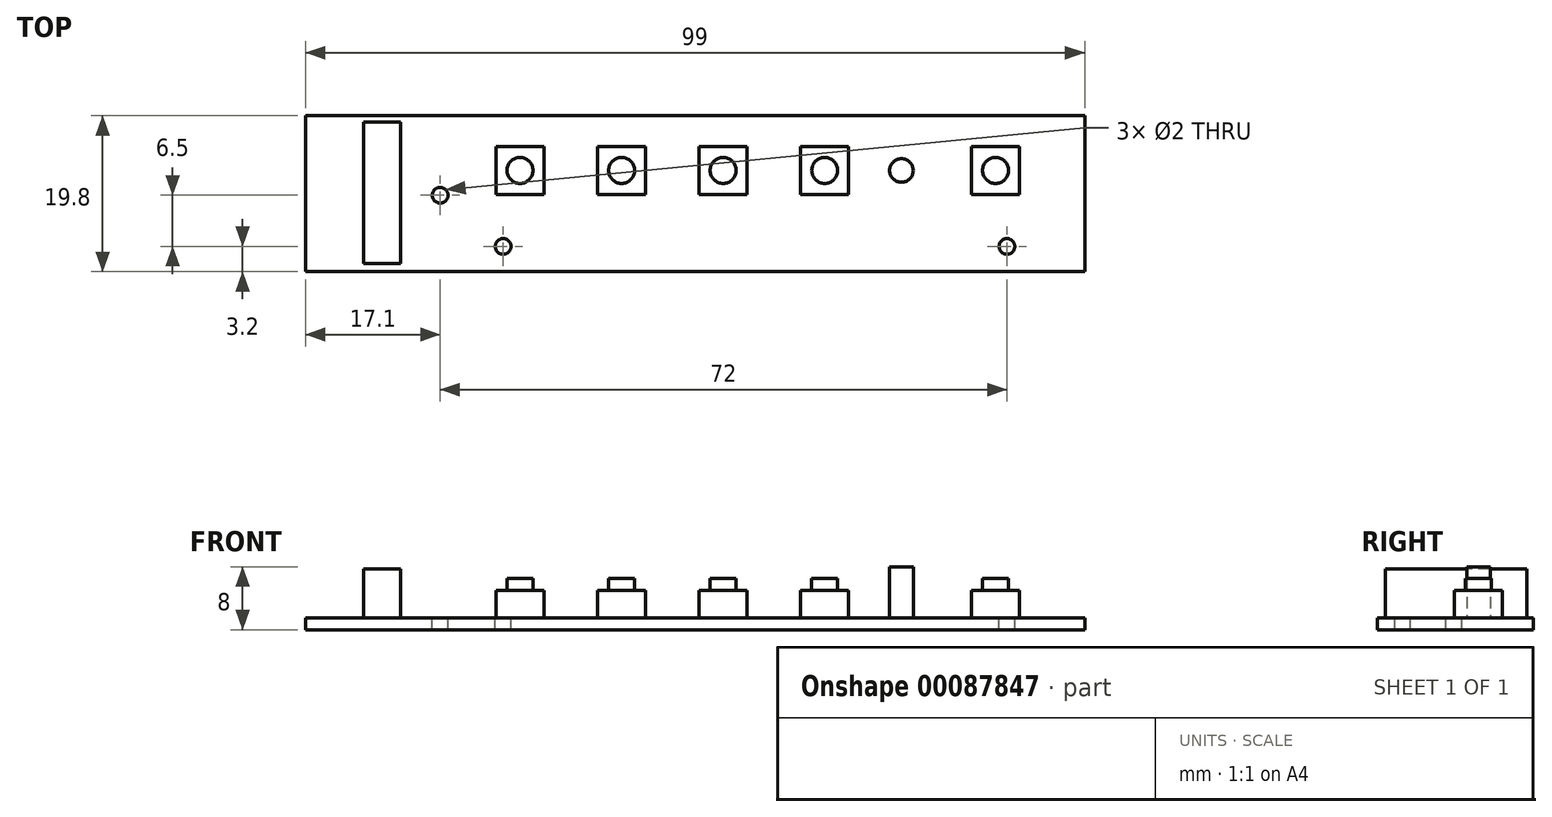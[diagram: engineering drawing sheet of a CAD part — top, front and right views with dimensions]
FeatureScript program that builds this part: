
annotation { "Feature Type Name" : "Feature", "Feature Type Description" : "" }
export const myFeature = defineFeature(function(context is Context, id is Id, definition is map)
    precondition{}
    {
        {
            var Q0;
            Q0=qCreatedBy(makeId("Top.planeOp"),FACE);
            var sketch = newSketch(context, id + "F0", { "sketchPlane" : qUnion([Q0])});
            skLineSegment(sketch, "E0.bottom", {"start": v(49.5, -9.9) * mm, "end": v(-49.5, -9.9) * mm});
            skLineSegment(sketch, "E0.top", {"start": v(49.5, 9.9) * mm, "end": v(-49.5, 9.9) * mm});
            skLineSegment(sketch, "E0.left", {"start": v(49.5, -9.9) * mm, "end": v(49.5, 9.9) * mm});
            skLineSegment(sketch, "E0.right", {"start": v(-49.5, -9.9) * mm, "end": v(-49.5, 9.9) * mm});
            skSolve(sketch);
        }
        {
            var Q0;
            Q0=makeQuery(id+"F0.imprint","IMPRINT",FACE,{"disambiguationData":[TD([[makeQuery(id+"F0.imprint","IMPRINT",EDGE,{"derivedFrom":sQuery(id+"F0.wireOp",EDGE,"E0.bottom")}),-1.0]])]});
            extrude(context, id + "F1", {"entities" : qUnion([Q0]), "depth" : 1.5 * mm});
        }
        {
            var Q0;
            Q0=makeQuery(id+"F1.opExtrude","CAP_FACE",FACE,{"disambiguationData":[OSD([sQuery(id+"F0.wireOp",EDGE,"E0.bottom"),sQuery(id+"F0.wireOp",EDGE,"E0.top"),sQuery(id+"F0.wireOp",EDGE,"E0.left"),sQuery(id+"F0.wireOp",EDGE,"E0.right"),sQuery(id+"F0.wireOp",EDGE,"EM1GxXzF-sUce-n6ho-FuAj-uYBGyEnzLMqh.bottom"),sQuery(id+"F0.wireOp",EDGE,"EM1GxXzF-sUce-n6ho-FuAj-uYBGyEnzLMqh.top"),sQuery(id+"F0.wireOp",EDGE,"EM1GxXzF-sUce-n6ho-FuAj-uYBGyEnzLMqh.left"),sQuery(id+"F0.wireOp",EDGE,"EM1GxXzF-sUce-n6ho-FuAj-uYBGyEnzLMqh.right"),sQuery(id+"F0.wireOp",EDGE,"TAAQUbrZ-hhXo-rL07-H4ab-Ilz5XIWETSzo.bottom"),sQuery(id+"F0.wireOp",EDGE,"TAAQUbrZ-hhXo-rL07-H4ab-Ilz5XIWETSzo.top"),sQuery(id+"F0.wireOp",EDGE,"TAAQUbrZ-hhXo-rL07-H4ab-Ilz5XIWETSzo.left"),sQuery(id+"F0.wireOp",EDGE,"TAAQUbrZ-hhXo-rL07-H4ab-Ilz5XIWETSzo.right"),sQuery(id+"F0.wireOp",EDGE,"RI9FpCbe-QOzY-rb1g-gpo4-utPUCl339mpE.bottom"),sQuery(id+"F0.wireOp",EDGE,"RI9FpCbe-QOzY-rb1g-gpo4-utPUCl339mpE.top"),sQuery(id+"F0.wireOp",EDGE,"RI9FpCbe-QOzY-rb1g-gpo4-utPUCl339mpE.left"),sQuery(id+"F0.wireOp",EDGE,"RI9FpCbe-QOzY-rb1g-gpo4-utPUCl339mpE.right"),sQuery(id+"F0.wireOp",EDGE,"XgnqqEYY-D4AL-pzjO-DKwZ-mFuAI1jGzbyk.bottom"),sQuery(id+"F0.wireOp",EDGE,"XgnqqEYY-D4AL-pzjO-DKwZ-mFuAI1jGzbyk.top"),sQuery(id+"F0.wireOp",EDGE,"XgnqqEYY-D4AL-pzjO-DKwZ-mFuAI1jGzbyk.left"),sQuery(id+"F0.wireOp",EDGE,"XgnqqEYY-D4AL-pzjO-DKwZ-mFuAI1jGzbyk.right"),sQuery(id+"F0.wireOp",EDGE,"XhRzdWj0-tqoo-7SP3-nGuN-otO9eouQI54y.bottom"),sQuery(id+"F0.wireOp",EDGE,"XhRzdWj0-tqoo-7SP3-nGuN-otO9eouQI54y.top"),sQuery(id+"F0.wireOp",EDGE,"XhRzdWj0-tqoo-7SP3-nGuN-otO9eouQI54y.left"),sQuery(id+"F0.wireOp",EDGE,"XhRzdWj0-tqoo-7SP3-nGuN-otO9eouQI54y.right")])],"isStart":false});
            var sketch = newSketch(context, id + "F2", { "sketchPlane" : qUnion([Q0])});
            skPoint(sketch, "E1.middle", {"position": v(-1.2, -0.2) * mm});
            skLineSegment(sketch, "E2.bottom", {"start": v(41.2, -0.1) * mm, "end": v(35.1, -0.1) * mm});
            skLineSegment(sketch, "E2.top", {"start": v(41.2, 6) * mm, "end": v(35.1, 6) * mm});
            skLineSegment(sketch, "E2.left", {"start": v(41.2, -0.1) * mm, "end": v(41.2, 6) * mm});
            skLineSegment(sketch, "E2.right", {"start": v(35.1, -0.1) * mm, "end": v(35.1, 6) * mm});
            skPoint(sketch, "E2.middle", {"position": v(38.15, 2.95) * mm});
            skLineSegment(sketch, "E3.bottom", {"start": v(19.5, -0.1) * mm, "end": v(13.4, -0.1) * mm});
            skLineSegment(sketch, "E3.top", {"start": v(19.5, 6) * mm, "end": v(13.4, 6) * mm});
            skLineSegment(sketch, "E3.left", {"start": v(19.5, -0.1) * mm, "end": v(19.5, 6) * mm});
            skLineSegment(sketch, "E3.right", {"start": v(13.4, -0.1) * mm, "end": v(13.4, 6) * mm});
            skPoint(sketch, "E3.middle", {"position": v(16.45, 2.95) * mm});
            skLineSegment(sketch, "E4.bottom", {"start": v(6.6, -0.1) * mm, "end": v(0.5, -0.1) * mm});
            skLineSegment(sketch, "E4.top", {"start": v(6.6, 6) * mm, "end": v(0.5, 6) * mm});
            skLineSegment(sketch, "E4.left", {"start": v(6.6, -0.1) * mm, "end": v(6.6, 6) * mm});
            skLineSegment(sketch, "E4.right", {"start": v(0.5, -0.1) * mm, "end": v(0.5, 6) * mm});
            skPoint(sketch, "E4.middle", {"position": v(3.55, 2.95) * mm});
            skLineSegment(sketch, "E5.bottom", {"start": v(-6.3, -0.1) * mm, "end": v(-12.4, -0.1) * mm});
            skLineSegment(sketch, "E5.top", {"start": v(-6.3, 6) * mm, "end": v(-12.4, 6) * mm});
            skLineSegment(sketch, "E5.left", {"start": v(-6.3, -0.1) * mm, "end": v(-6.3, 6) * mm});
            skLineSegment(sketch, "E5.right", {"start": v(-12.4, -0.1) * mm, "end": v(-12.4, 6) * mm});
            skPoint(sketch, "E5.middle", {"position": v(-9.35, 2.95) * mm});
            skLineSegment(sketch, "E6.bottom", {"start": v(-19.2, -0.1) * mm, "end": v(-25.3, -0.1) * mm});
            skLineSegment(sketch, "E6.top", {"start": v(-19.2, 6) * mm, "end": v(-25.3, 6) * mm});
            skLineSegment(sketch, "E6.left", {"start": v(-19.2, -0.1) * mm, "end": v(-19.2, 6) * mm});
            skLineSegment(sketch, "E6.right", {"start": v(-25.3, -0.1) * mm, "end": v(-25.3, 6) * mm});
            skPoint(sketch, "E6.middle", {"position": v(-22.25, 2.95) * mm});
            skSolve(sketch);
        }
        {
            var Q0;
            Q0 = qSketchRegion(id + "F2", true);
            extrude(context, id + "F3", {"entities" : qUnion([Q0]), "operationType" : NewBodyOperationType.ADD, "depth" : 3.5 * mm});
        }
        {
            var Q0;
            Q0=makeQuery(id+"F3.opExtrude","CAP_FACE",FACE,{"disambiguationData":[OSD([sQuery(id+"F2.wireOp",EDGE,"E2.bottom"),sQuery(id+"F2.wireOp",EDGE,"E2.top"),sQuery(id+"F2.wireOp",EDGE,"E2.left"),sQuery(id+"F2.wireOp",EDGE,"E2.right")])],"isStart":false});
            var sketch = newSketch(context, id + "F4", { "sketchPlane" : qUnion([Q0])});
            skCircle(sketch, "E7", {"center": v(-22.25, 2.95) * mm, "radius": 1.65 * mm});
            skPoint(sketch, "E7.centerSnap0", {"position": v(-22.25, -0.1) * mm});
            skPoint(sketch, "E7.centerSnap1", {"position": v(-19.2, 2.95) * mm});
            skCircle(sketch, "E8", {"center": v(-9.35, 2.95) * mm, "radius": 1.65 * mm});
            skPoint(sketch, "E8.centerSnap0", {"position": v(-9.35, -0.1) * mm});
            skPoint(sketch, "E8.centerSnap1", {"position": v(-12.4, 2.95) * mm});
            skCircle(sketch, "E9", {"center": v(3.55, 2.95) * mm, "radius": 1.65 * mm});
            skPoint(sketch, "E9.centerSnap0", {"position": v(3.55, -0.1) * mm});
            skPoint(sketch, "E9.centerSnap1", {"position": v(0.5, 2.95) * mm});
            skCircle(sketch, "E10", {"center": v(16.45, 2.95) * mm, "radius": 1.65 * mm});
            skPoint(sketch, "E10.centerSnap0", {"position": v(16.45, -0.1) * mm});
            skPoint(sketch, "E10.centerSnap1", {"position": v(13.4, 2.95) * mm});
            skCircle(sketch, "E11", {"center": v(38.15, 2.95) * mm, "radius": 1.65 * mm});
            skPoint(sketch, "E11.centerSnap0", {"position": v(35.1, 2.95) * mm});
            skPoint(sketch, "E11.centerSnap1", {"position": v(38.15, -0.1) * mm});
            skSolve(sketch);
        }
        {
            var Q0;
            Q0 = qSketchRegion(id + "F4", true);
            extrude(context, id + "F5", {"entities" : qUnion([Q0]), "operationType" : NewBodyOperationType.ADD, "depth" : 1.5 * mm});
        }
        {
            var Q0;
            Q0=makeQuery(id+"F1.opExtrude","CAP_FACE",FACE,{"disambiguationData":[OSD([sQuery(id+"F0.wireOp",EDGE,"E0.bottom"),sQuery(id+"F0.wireOp",EDGE,"E0.top"),sQuery(id+"F0.wireOp",EDGE,"E0.left"),sQuery(id+"F0.wireOp",EDGE,"E0.right")])],"isStart":false});
            var sketch = newSketch(context, id + "F6", { "sketchPlane" : qUnion([Q0])});
            skCircle(sketch, "E12", {"center": v(26.2, 2.95) * mm, "radius": 1.5 * mm});
            skPoint(sketch, "E12.centerSnap0", {"position": v(35.1, 2.95) * mm});
            skSolve(sketch);
        }
        {
            var Q0;
            Q0 = qSketchRegion(id + "F6", true);
            extrude(context, id + "F7", {"entities" : qUnion([Q0]), "operationType" : NewBodyOperationType.ADD, "depth" : 6.5 * mm});
        }
        {
            var Q0;
            Q0=makeQuery(id+"F1.opExtrude","CAP_FACE",FACE,{"disambiguationData":[OSD([sQuery(id+"F0.wireOp",EDGE,"E0.bottom"),sQuery(id+"F0.wireOp",EDGE,"E0.top"),sQuery(id+"F0.wireOp",EDGE,"E0.left"),sQuery(id+"F0.wireOp",EDGE,"E0.right")])],"isStart":false});
            var sketch = newSketch(context, id + "F8", { "sketchPlane" : qUnion([Q0])});
            skLineSegment(sketch, "E13.bottom", {"start": v(-42.1, 9.1) * mm, "end": v(-37.4, 9.1) * mm});
            skLineSegment(sketch, "E13.top", {"start": v(-42.1, -8.9) * mm, "end": v(-37.4, -8.9) * mm});
            skLineSegment(sketch, "E13.left", {"start": v(-42.1, 9.1) * mm, "end": v(-42.1, -8.9) * mm});
            skLineSegment(sketch, "E13.right", {"start": v(-37.4, 9.1) * mm, "end": v(-37.4, -8.9) * mm});
            skSolve(sketch);
        }
        {
            var Q0;
            Q0 = qSketchRegion(id + "F8", true);
            extrude(context, id + "F9", {"entities" : qUnion([Q0]), "operationType" : NewBodyOperationType.ADD, "depth" : 6.2 * mm});
        }
        {
            var Q0;
            Q0=makeQuery(id+"F1.opExtrude","CAP_FACE",FACE,{"disambiguationData":[OSD([sQuery(id+"F0.wireOp",EDGE,"E0.bottom"),sQuery(id+"F0.wireOp",EDGE,"E0.top"),sQuery(id+"F0.wireOp",EDGE,"E0.left"),sQuery(id+"F0.wireOp",EDGE,"E0.right")])],"isStart":false});
            var sketch = newSketch(context, id + "F10", { "sketchPlane" : qUnion([Q0])});
            skCircle(sketch, "E14", {"center": v(-24.4, -6.7) * mm, "radius": 1 * mm});
            skCircle(sketch, "E15", {"center": v(-32.4, -0.2) * mm, "radius": 1 * mm});
            skCircle(sketch, "E16", {"center": v(39.6, -6.7) * mm, "radius": 1 * mm});
            skSolve(sketch);
        }
        {
            var Q0;
            Q0 = qSketchRegion(id + "F10", true);
            extrude(context, id + "F11", {"entities" : qUnion([Q0]), "operationType" : NewBodyOperationType.REMOVE, "endBound" : BoundingType.THROUGH_ALL, "oppositeDirection" : true, "depth" : 25 * mm});
        }
    });
